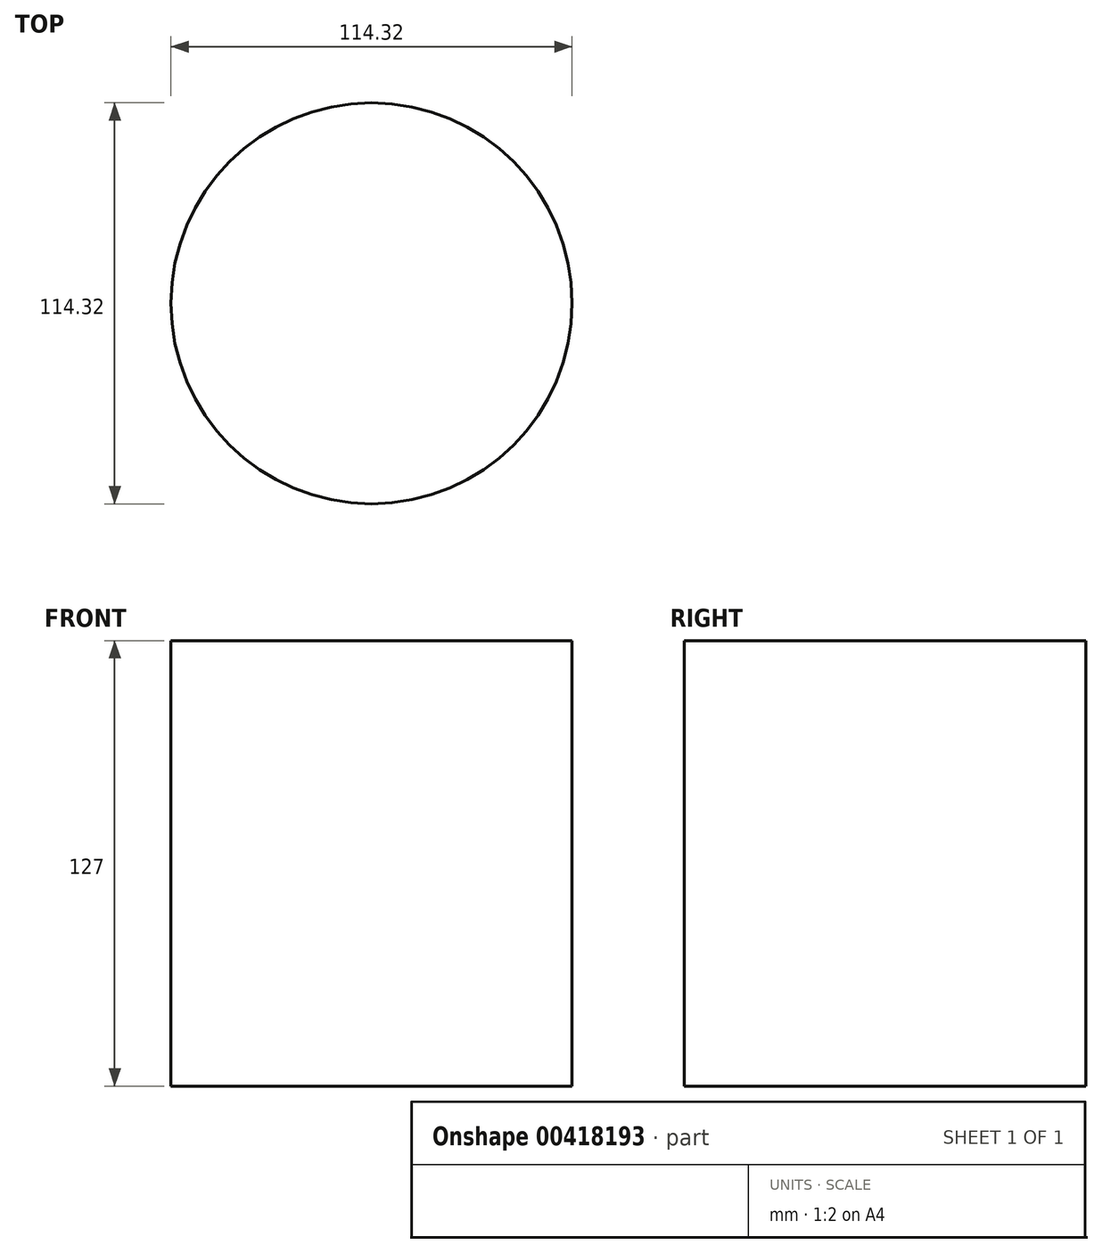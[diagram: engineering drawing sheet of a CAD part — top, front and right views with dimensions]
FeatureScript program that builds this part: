
annotation { "Feature Type Name" : "Feature", "Feature Type Description" : "" }
export const myFeature = defineFeature(function(context is Context, id is Id, definition is map)
    precondition{}
    {
        {
            var Q0;
            Q0=qCreatedBy(makeId("Top.planeOp"),FACE);
            var sketch = newSketch(context, id + "F0", { "sketchPlane" : qUnion([Q0])});
            skCircle(sketch, "E0", {"center": v(0, 0) * mm, "radius": 57.16 * mm});
            skSolve(sketch);
        }
        {
            var Q0;
            Q0 = qSketchRegion(id + "F0", true);
            extrude(context, id + "F1", {"entities" : qUnion([Q0]), "depth" : 127 * mm});
        }
    });
